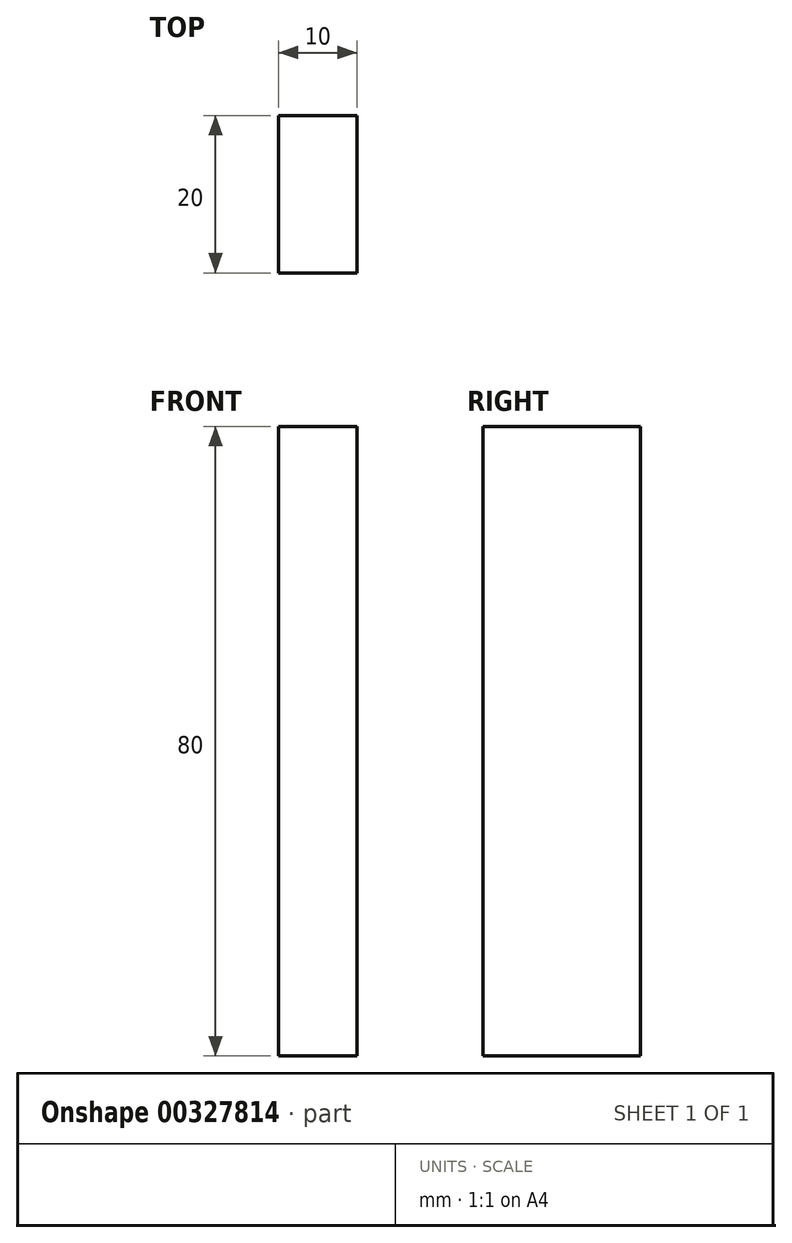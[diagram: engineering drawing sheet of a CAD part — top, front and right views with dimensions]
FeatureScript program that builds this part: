
annotation { "Feature Type Name" : "Feature", "Feature Type Description" : "" }
export const myFeature = defineFeature(function(context is Context, id is Id, definition is map)
    precondition{}
    {
        {
            var Q0;
            Q0=qCreatedBy(makeId("Front.planeOp"),FACE);
            var sketch = newSketch(context, id + "F0", { "sketchPlane" : qUnion([Q0])});
            skLineSegment(sketch, "E0.bottom", {"start": v(57.33, 42.56) * mm, "end": v(47.33, 42.56) * mm});
            skLineSegment(sketch, "E0.top", {"start": v(57.33, -37.44) * mm, "end": v(47.33, -37.44) * mm});
            skLineSegment(sketch, "E0.left", {"start": v(57.33, 42.56) * mm, "end": v(57.33, -37.44) * mm});
            skLineSegment(sketch, "E0.right", {"start": v(47.33, 42.56) * mm, "end": v(47.33, -37.44) * mm});
            skSolve(sketch);
        }
        {
            var Q0;
            Q0=makeQuery(id+"F0.imprint","IMPRINT",FACE,{"disambiguationData":[TD([[makeQuery(id+"F0.imprint","IMPRINT",EDGE,{"derivedFrom":sQuery(id+"F0.wireOp",EDGE,"E0.bottom")}),1.0]])]});
            extrude(context, id + "F1", {"entities" : qUnion([Q0]), "depth" : 20 * mm});
        }
    });
